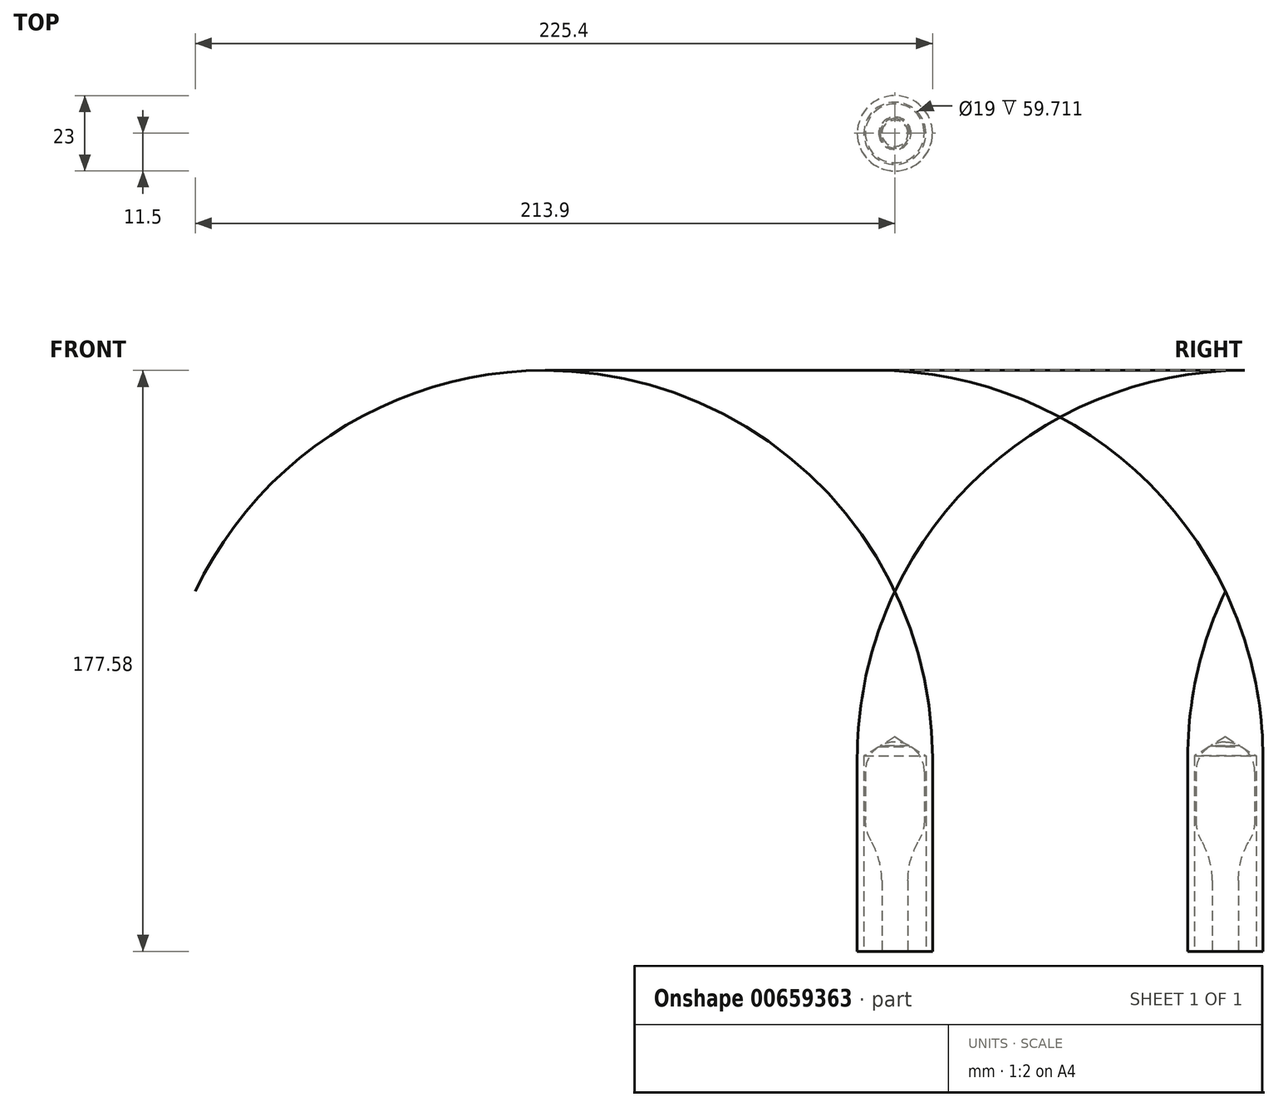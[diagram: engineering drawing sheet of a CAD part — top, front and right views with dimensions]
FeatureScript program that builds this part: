
annotation { "Feature Type Name" : "Feature", "Feature Type Description" : "" }
export const myFeature = defineFeature(function(context is Context, id is Id, definition is map)
    precondition{}
    {
        {
            var Q0;
            Q0=qCreatedBy(makeId("Right.planeOp"),FACE);
            var sketch = newSketch(context, id + "F0", { "sketchPlane" : qUnion([Q0])});
            skLineSegment(sketch, "E0", {"start": v(0, 0) * mm, "end": v(0, 64) * mm});
            skLineSegment(sketch, "E1", {"start": v(9, 55) * mm, "end": v(9, 40.2) * mm});
            skLineSegment(sketch, "E2", {"start": v(0, 0) * mm, "end": v(4, 0) * mm});
            skLineSegment(sketch, "E3", {"start": v(4, 0) * mm, "end": v(4, 21.6) * mm});
            skArc(sketch, "E4", {"start": v(9, 55) * mm, "mid": v(6.36, 61.36) * mm, "end": v(0, 64) * mm});
            skArc(sketch, "E5", {"start": v(7.25, 33.7) * mm, "mid": v(8.56, 36.83) * mm, "end": v(9, 40.2) * mm});
            skArc(sketch, "E6", {"start": v(7.25, 33.7) * mm, "mid": v(4.83, 27.87) * mm, "end": v(4, 21.6) * mm});
            skSolve(sketch);
        }
        {
            var Q0;
            Q0=makeQuery(id+"F0.imprint","IMPRINT",FACE,{"disambiguationData":[TD([[makeQuery(id+"F0.imprint","IMPRINT",EDGE,{"derivedFrom":sQuery(id+"F0.wireOp",EDGE,"E0")}),-1.0]])]});
            var Q1;
            Q1=sQuery(id+"F0.wireOp",EDGE,"E0");
            revolve(context, id + "F1", {"entities" : qUnion([Q0]), "axis" : qUnion([Q1]), "revolveType" : RevolveType.FULL});
        }
        {
            var Q0;
            Q0=qCreatedBy(makeId("Right.planeOp"),FACE);
            var sketch = newSketch(context, id + "F2", { "sketchPlane" : qUnion([Q0])});
            skLineSegment(sketch, "E7", {"start": v(0, 65.57) * mm, "end": v(9.5, 59.71) * mm});
            skLineSegment(sketch, "E8", {"start": v(9.5, 59.71) * mm, "end": v(9.5, 0) * mm});
            skLineSegment(sketch, "E9", {"start": v(9.5, 0) * mm, "end": v(11.5, 0) * mm});
            skLineSegment(sketch, "E10", {"start": v(11.5, 0) * mm, "end": v(11.5, 59.13) * mm});
            skLineSegment(sketch, "E11", {"start": v(0, 0) * mm, "end": v(0, 110.04) * mm});
            skArc(sketch, "E12", {"start": v(11.5, 59.13) * mm, "mid": v(8.59, 85.23) * mm, "end": v(0, 110.04) * mm});
            skSolve(sketch);
        }
        {
            var Q0;
            {var subQ0=sQuery(id+"F2.wireOp",EDGE,"E7");Q0=makeQuery(id+"F2.imprint","IMPRINT",FACE,{"disambiguationData":[TD([[makeQuery(id+"F2.imprint","IMPRINT",EDGE,{"derivedFrom":subQ0}),1.0]])]});}
            var Q1;
            Q1=sQuery(id+"F2.wireOp",EDGE,"E11");
            revolve(context, id + "F3", {"operationType" : NewBodyOperationType.ADD, "entities" : qUnion([Q0]), "axis" : qUnion([Q1]), "revolveType" : RevolveType.FULL});
        }
    });
